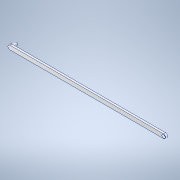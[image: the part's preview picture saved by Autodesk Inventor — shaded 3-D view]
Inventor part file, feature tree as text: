
AUTODESK INVENTOR PART (.ipt)
format: ipt  version: 2021 (Build 250183000, 183)  size: 111,616 bytes
history: native  units: in
note: dims shown in document units (in); Inventor stores cm internally (conversion verified against a paired STEP export)
features: extrude x3, sketch x3, other x1
ambient origin geometry x8: Origin, YZ Plane, XZ Plane, XY Plane, X Axis, Y Axis, Z Axis, Center Point
bodies: Body1 (feature_tree)
feature tree (7):
  other  "Sólido1"
  extrude  "Extrusión1"  Depth=0.25in
  extrude  "Extrusión2"  Depth=0.2756in TaperAngle=0.0deg
  extrude  "Extrusión3"  Depth=0.25in
  sketch  "Boceto1"  dims[d0=0.25in d3=0.25in]
  sketch  "Boceto2"  dims[d4=0.125in d5=0.0in d8=0.2756in d9=0.0in]
  sketch  "Boceto3"  dims[d10=0.25in d11=0.0197in d12=0.1969in d13=0.0in d14=19.685in d15=0.0344in]
